# Revit family: xHand_Dryer-Recessed-Bobrick-Trimline-B-3725
name_source: partatom
category: Specialty Equipment
revit_build: Autodesk Revit 2014 (Build: 20130308_1515(x64)
units: mm (PartAtom-declared; Revit-internal decimal feet)

## types (2) — shared parameters
ADA Compliant = Yes
Assembly Code = E1090
Default Elevation = 48 "
Depth = 6 "
Description = Trimline Recessed Mounted Warm Air Hand Dryer
Frequency = 60 Hz
Height = 24 "
Installation Type = Recessed Mounted
Manufacturer = Bobrick
Material = Stainless Steel-Bobrick-Type 304-Satin
Phase = 1
Price = Prices may vary. Please consult Manufacturer Representative for most up-to-date price list.
Product Documentation Link = http://www.bobrick.com
Product Page URL = http://www.bobrick.com
Specification = B-3725 ADA Recessed Hand Dryer, Type 304 Satin-finish, stainless steel with a low profile contemporary design. Dryer delivers a 17-second dry time at a mere 72dBA and sustainable 1000 Watts of power. 115V AC, 8.5 Amp, 50/60 Hz, 1000 Watts, Single Phase, cULus Listed, or 208-240V AC, 4.0-4.4 Amp, 50/60 Hz, 1000 Watts, Single Phase, cULus Listed and CE marked.
URL = http://www.bobrick.com
Warranty Information = 3 Year Limited Warranty
Wattage = 1000 W
Width = 12 "

## per-type parameters (varying)
| type | Amperage | Connection Description | Voltage |
| B-3725 115V | 9 A | 115V Electrical Connection | 115 V |
| B-3725 230V | 4 A | 230V Electrical Connection | 230 V |

note: column(s) folded — value = type name in every type: Model

## geometry (parser evidence)
native form markers: Sweep x2
no freeform markers — native parametric forms only
